# Revit family: Ytong nenosné překlady
name_source: partatom
category: Structural Framing
units: mm (PartAtom-declared; Revit-internal decimal feet)

## family parameters
Always export as geometry = No
Always vertical = Yes
Cut with Voids When Loaded = No
Material for Model Behavior = Other
Section Shape = Not Defined
Shared = Yes
Show family pre-cut in plan views = Yes
Structural Framing Length Roundoff = 0 mm
Work Plane-Based = No

## types (1)
- Ytong nenosné překlady
    Autor = BIM Technology s.r.o.
    Description = Pórobetonové prvky vyztužené betonářskou výztuží
    Faktor difúzního odporu μ (EN 1745) = 5/10
    Fire Rating = R 60
    Hláška při nenalezení = Překročena maximální světlost otvoru!
    IfcExportAs = IfcBeam
    IfcExportType = LINTEL
    Krátký popis = Pórobetonové prvky vyztužené betonářskou výztuží
    Manufacturer = Ytong
    Materiál = pórobeton AAC 4,5-600
    Max. průměrná objemová hmotnost v suchém stavu (EN 772-13) [kg/m3] = 600
    Minimální délka nosníku = 1250 mm  [stored 4.10105 ft]
    Modul pružnosti Eb [N/mm2] = 2250
    Měrná tepelná kapacita c (EN 1745) = 1.0500 J/(g·°C)
    Normalizovaná pevnost fb [N/mm2] = 5
    Název tabulky = Ytong nenosné překlady
    Odkaz na DoP = https://storefrontapi.commerce.xella.com
    Odkaz na stavební postup = https://storefrontapi.commerce.xella.com
    Odkaz na technický list = https://storefrontapi.commerce.xella.com
    Odkaz na web = https://www.xella.cz
    Přídržnost [N/mm2] = 0.3
    Skupina prvků = Překlad
    Součinitel tep. vodivosti lambda = 0.1650 W/(m·K)
    Součinitel tepelné vodivosti – deklarovaná hodnota λ10,dry = 0.1500 W/(m·K)
    Součinitel tepelného přetvoření αb [1/K] = 8e-06
    URL = https://www.xella.cz
    Vlhkostní přetvoření ε [mm/m] = 0.2
    Zobrazit ve výkazech = Yes

note: [stored X ft] marks values corroborated as IEEE doubles in the binary element streams (Revit-internal decimal feet)
